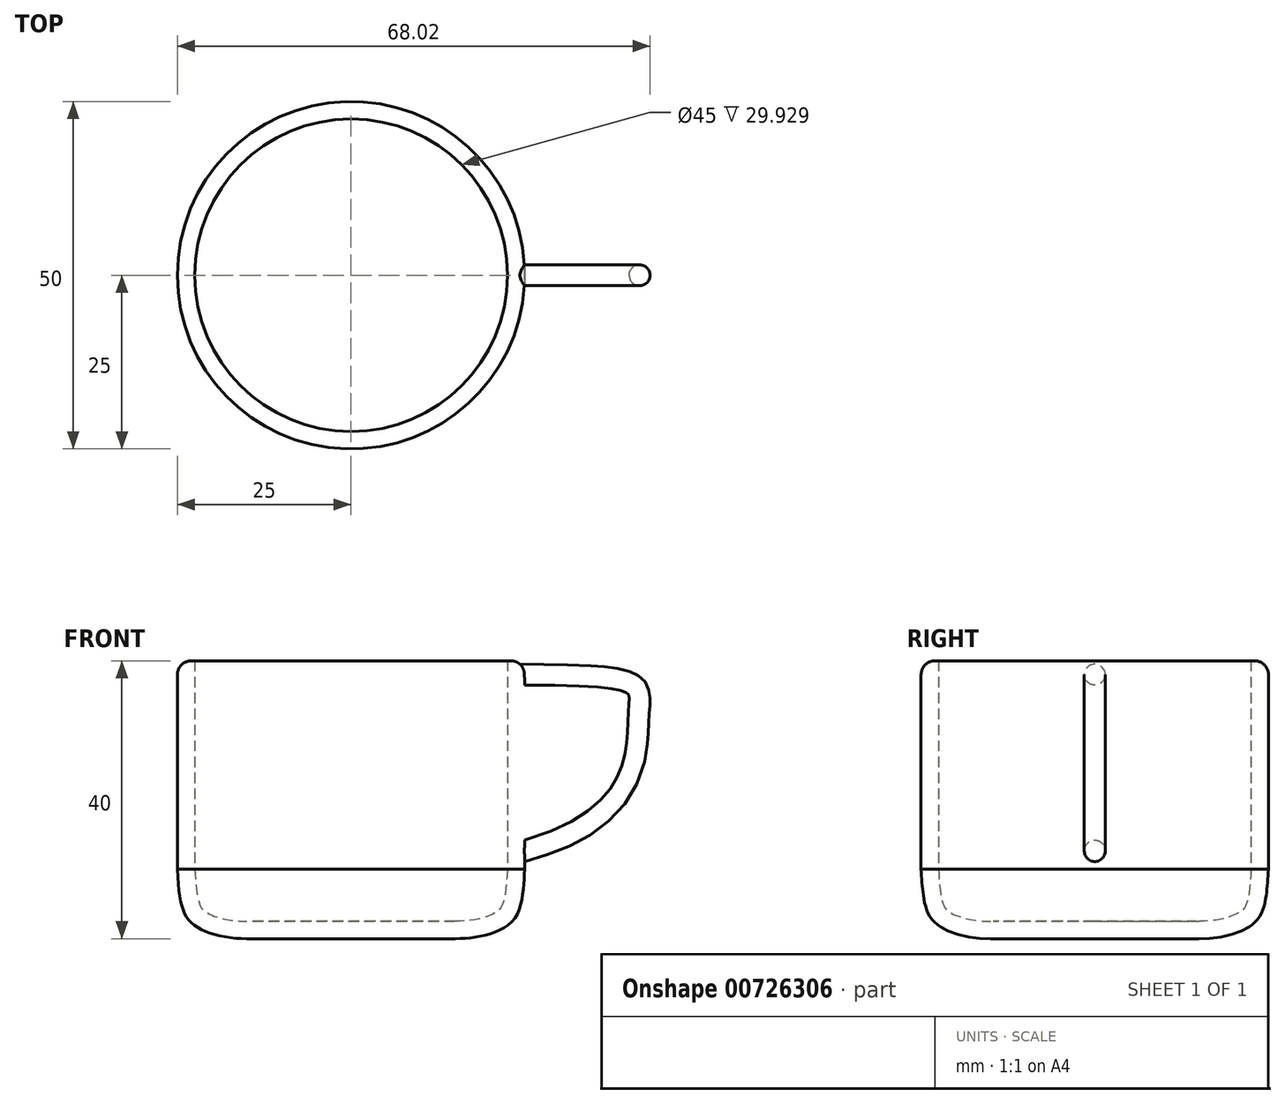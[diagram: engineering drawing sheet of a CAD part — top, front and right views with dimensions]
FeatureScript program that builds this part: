
annotation { "Feature Type Name" : "Feature", "Feature Type Description" : "" }
export const myFeature = defineFeature(function(context is Context, id is Id, definition is map)
    precondition{}
    {
        {
            var Q0;
            Q0=qCreatedBy(makeId("Front.planeOp"),FACE);
            var sketch = newSketch(context, id + "F0", { "sketchPlane" : qUnion([Q0])});
            skLineSegment(sketch, "E0", {"start": v(15, 0) * mm, "end": v(0, 0) * mm});
            skLineSegment(sketch, "E1", {"start": v(0, 0) * mm, "end": v(0, 40) * mm});
            skLineSegment(sketch, "E2", {"start": v(0, 40) * mm, "end": v(25, 40) * mm});
            skLineSegment(sketch, "E3", {"start": v(25, 40) * mm, "end": v(25, 10) * mm});
            skFitSpline(sketch, "E4", {"points": [v(25, 10) * mm, v(22.78, 2.12) * mm, v(15, 0) * mm], "startDerivative": vector(-1.53, -27.05) * mm, "endDerivative": vector(-19.07, 0) * mm});
            skSolve(sketch);
        }
        {
            var Q0;
            Q0 = qSketchRegion(id + "F0", true);
            var Q1;
            Q1=sQuery(id+"F0.wireOp",EDGE,"E1");
            revolve(context, id + "F1", {"surfaceOperationType" : NewSurfaceOperationType.NEW, "entities" : qUnion([Q0]), "axis" : qUnion([Q1]), "revolveType" : RevolveType.FULL});
        }
        {
            var Q0;
            Q0=makeQuery(id+"F1.opRevolve","SWEPT_EDGE",EDGE,{"disambiguationData":[OSD([sQuery(id+"F0.wireOp",EDGE,"E2"),sQuery(id+"F0.wireOp",EDGE,"E3")])]});
            fillet(context, id + "F2", {"entities" : qUnion([Q0]), "radius" : 2 * mm, "tangentPropagation" : true, "allowEdgeOverflow" : false});
        }
        {
            var Q0;
            Q0=qCreatedBy(makeId("Right.planeOp"),FACE);
            var sketch = newSketch(context, id + "F3", { "sketchPlane" : qUnion([Q0])});
            skCircle(sketch, "E5", {"center": v(0, 38) * mm, "radius": 1.5 * mm});
            skSolve(sketch);
        }
        {
            var Q0;
            Q0=qCreatedBy(makeId("Front.planeOp"),FACE);
            var sketch = newSketch(context, id + "F4", { "sketchPlane" : qUnion([Q0])});
            skFitSpline(sketch, "E6", {"points": [v(0, 38) * mm, v(41.4, 32.15) * mm, v(0, 10) * mm], "startDerivative": vector(270.9, 0) * mm, "endDerivative": vector(-248.48, 0) * mm});
            skSolve(sketch);
        }
        {
            var Q0;
            Q0 = qSketchRegion(id + "F3", true);
            var Q1;
            Q1 = qConstructionFilter(qBodyType(qCreatedBy(id + "F4" ,EDGE), BodyType.WIRE), ConstructionObject.NO);
            sweep(context, id + "F5", {"operationType" : NewBodyOperationType.ADD, "profiles" : qUnion([Q0]), "path" : qUnion([Q1])});
        }
        {
            var Q0;
            Q0=makeQuery(id+"F1.opRevolve","SWEPT_FACE",FACE,{"disambiguationData":[OSD([sQuery(id+"F0.wireOp",EDGE,"E2")])]});
            shell(context, id + "F6", {"entities" : qUnion([Q0]), "thickness" : 2.5 * mm});
        }
    });
